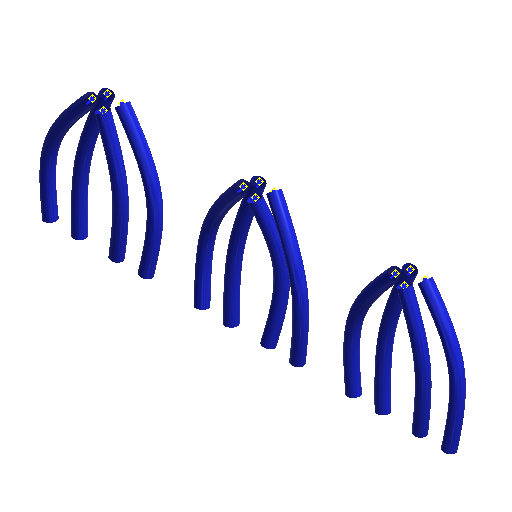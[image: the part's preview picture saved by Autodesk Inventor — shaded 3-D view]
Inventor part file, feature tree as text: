
AUTODESK INVENTOR PART (.ipt)
format: ipt  version: 2022 (Build 260153000, 153)  size: 660,992 bytes
history: native  units: mm (DEFAULTED — no unit token found)
features: other x60, plane x12, sketch x12, sweep x12
ambient origin geometry x8: Origin, YZ Plane, XZ Plane, XY Plane, X Axis, Y Axis, Z Axis, Center Point
bodies: Body1 (feature_tree), Body2 (feature_tree), Body3 (feature_tree), Body4 (feature_tree), Body5 (feature_tree), Body6 (feature_tree), Body7 (feature_tree), Body8 (feature_tree), Body9 (feature_tree), Body10 (feature_tree), Body11 (feature_tree), Body12 (feature_tree)
feature tree (96):
  other  "Work Point1"
  other  "Work Point2"
  other  "Wire1"
  other  "Work Point3"
  other  "Work Point4"
  other  "Wire2"
  other  "Work Point5"
  other  "Work Point6"
  other  "Wire3"
  other  "Work Point7"
  other  "Work Point8"
  other  "Wire4"
  other  "Work Point9"
  other  "Work Point10"
  other  "Wire5"
  other  "Work Point11"
  other  "Work Point12"
  other  "Wire6"
  other  "Work Point13"
  other  "Work Point14"
  other  "Wire7"
  other  "Work Point15"
  other  "Work Point16"
  other  "Wire8"
  other  "Work Point17"
  other  "Work Point18"
  other  "Wire9"
  other  "Work Point19"
  other  "Work Point20"
  other  "Wire10"
  other  "Work Point21"
  other  "Work Point22"
  other  "Wire11"
  other  "Work Point23"
  other  "Work Point24"
  other  "Wire12"
  plane  "Work Plane1"
  plane  "Work Plane2"
  plane  "Work Plane3"
  plane  "Work Plane4"
  plane  "Work Plane5"
  plane  "Work Plane6"
  plane  "Work Plane7"
  plane  "Work Plane8"
  plane  "Work Plane9"
  plane  "Work Plane10"
  plane  "Work Plane11"
  plane  "Work Plane12"
  other  "Work Point37"
  other  "Work Point38"
  other  "Work Point39"
  other  "Work Point40"
  other  "Work Point41"
  other  "Work Point43"
  other  "Work Point44"
  other  "Work Point45"
  other  "Work Point46"
  other  "Work Point47"
  other  "Work Point48"
  other  "Work Point49"
  sketch  "Sketch1"  dims[d0=0.0mm d1=0.0mm d2=0.0mm d3=0.0mm]
  other  "Srf1"
  sketch  "Sketch2"  dims[d4=0.0mm d5=0.0mm d6=0.0mm d7=0.0mm]
  other  "Srf2"
  sketch  "Sketch3"  dims[d8=0.0mm d9=0.0mm d10=0.0mm d11=0.0mm]
  other  "Srf3"
  sketch  "Sketch4"  dims[d12=0.0mm d13=0.0mm d14=0.0mm d15=0.0mm]
  other  "Srf4"
  sketch  "Sketch5"  dims[d16=0.0mm d17=0.0mm d18=0.0mm d19=0.0mm]
  other  "Srf5"
  sketch  "Sketch6"  dims[d20=0.0mm d21=0.0mm d22=0.0mm d23=0.0mm]
  other  "Srf6"
  sketch  "Sketch7"
  other  "Srf7"
  sketch  "Sketch8"
  other  "Srf8"
  sketch  "Sketch9"
  other  "Srf9"
  sketch  "Sketch10"
  other  "Srf10"
  sketch  "Sketch11"
  other  "Srf11"
  sketch  "Sketch12"
  other  "Srf12"
  sweep  "SweepSrf1"
  sweep  "SweepSrf2"
  sweep  "SweepSrf3"
  sweep  "SweepSrf4"
  sweep  "SweepSrf5"
  sweep  "SweepSrf6"
  sweep  "SweepSrf7"
  sweep  "SweepSrf8"
  sweep  "SweepSrf9"
  sweep  "SweepSrf10"
  sweep  "SweepSrf11"
  sweep  "SweepSrf12"
